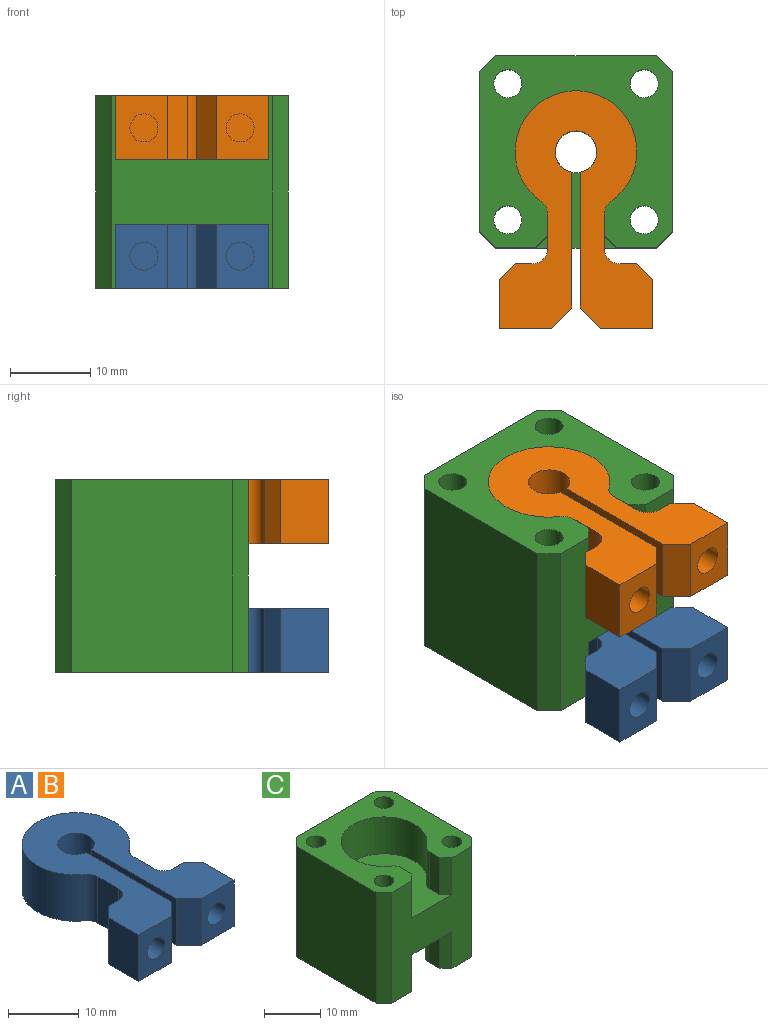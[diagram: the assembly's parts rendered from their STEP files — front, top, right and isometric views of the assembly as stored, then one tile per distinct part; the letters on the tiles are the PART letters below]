
ASSEMBLY  parts=3 mates=3
PART A: 26 faces, bbox 19x29.6x8 mm
  f0: cylinder r=7.6mm len=15.2mm, axis (0,0,1), area 307.8mm2, adj f1,f3,f24,f25
  f1: plane 29.6x19mm, normal (0,0,-1), area 331.4mm2, adj f0,f2,f4,f5,f6,f7,f8,f9
  f2: cylinder r=2.6mm len=8mm, axis (0,0,1), area 122.6mm2, adj f1,f3,f5,f7
  f3: plane 29.6x19mm, normal (0,0,1), area 331.4mm2, adj f0,f2,f4,f5,f6,f7,f8,f9
  f4: plane 8x6.5mm, normal (0,-1,0), area 42.4mm2, adj f1,f3,f11,f20,f23
  f5: plane 16.95x8mm, normal (1,0,0), area 135.6mm2, adj f1,f2,f3,f23
  f6: plane 8x4.13mm, normal (-1,0,0), area 33.1mm2, adj f1,f3,f15,f25
  f7: plane 16.95x8mm, normal (-1,0,0), area 135.6mm2, adj f1,f2,f3,f22
  f8: plane 8x6.5mm, normal (0,-1,0), area 42.4mm2, adj f1,f3,f12,f18,f22
  f9: plane 8x4.13mm, normal (1,0,0), area 33.1mm2, adj f1,f3,f14,f24
  f10: plane 8x2mm, normal (0,1,0), area 16mm2, adj f1,f3,f15,f17
  f11: plane 8x6mm, normal (-1,0,0), area 48mm2, adj f1,f3,f4,f17
  f12: plane 8x6mm, normal (1,0,0), area 48mm2, adj f1,f3,f8,f16
  f13: plane 8x2mm, normal (0,1,0), area 16mm2, adj f1,f3,f14,f16
  f14: cylinder r=2mm len=8mm, axis (0,0,-1), area 25.1mm2, adj f1,f3,f9,f13
  f15: cylinder r=2mm len=8mm, axis (0,0,-1), area 25.1mm2, adj f1,f3,f6,f10
  f16: plane 8x2mm, normal (0.71,0.71,0), area 22.6mm2, adj f1,f3,f12,f13
  f17: plane 8x2mm, normal (-0.71,0.71,0), area 22.6mm2, adj f1,f3,f10,f11
  f18: cylinder r=1.75mm len=5mm, axis (0,-1,0), area 55mm2, adj f8,f19
  f19: plane 3.5x3.5mm, normal (0,-1,0), area 9.6mm2, adj f18
  f20: cylinder r=1.75mm len=5mm, axis (0,-1,0), area 55mm2, adj f4,f21
  f21: plane 3.5x3.5mm, normal (0,-1,0), area 9.6mm2, adj f20
  f22: plane 8x2.5mm, normal (-0.71,-0.71,0), area 28.3mm2, adj f1,f3,f7,f8
  f23: plane 8x2.5mm, normal (0.71,-0.71,0), area 28.3mm2, adj f1,f3,f4,f5
  f24: cylinder r=2mm len=8mm, axis (0,0,1), area 15.4mm2, adj f0,f1,f3,f9
  f25: cylinder r=2mm len=8mm, axis (0,0,1), area 15.4mm2, adj f0,f1,f3,f6
PART B: same geometry as A
PART C: 31 faces, bbox 24x24x24 mm
  f0: cylinder r=2.6mm len=8mm, axis (0,0,-1), area 130.7mm2, adj f13,f20
  f1: plane 24x20mm, normal (0,-1,0), area 320mm2, adj f2,f6,f9,f10,f13,f20,f23,f24
  f2: plane 24x24mm, normal (0,0,-1), area 319.2mm2, adj f1,f3,f4,f5,f7,f8,f9,f10
  f3: plane 24x20mm, normal (-1,0,0), area 480mm2, adj f2,f6,f8,f10
  f4: plane 24x20mm, normal (1,0,0), area 480mm2, adj f2,f6,f7,f9
  f5: plane 24x20mm, normal (0,1,0), area 480mm2, adj f2,f6,f7,f8
  f6: plane 24x24mm, normal (0,0,1), area 312.7mm2, adj f1,f3,f4,f5,f7,f8,f9,f10
  f7: plane 24x2mm, normal (0.71,0.71,0), area 67.9mm2, adj f2,f4,f5,f6
  f8: plane 24x2mm, normal (-0.71,0.71,0), area 67.9mm2, adj f2,f3,f5,f6
  f9: plane 24x2mm, normal (0.71,-0.71,0), area 67.9mm2, adj f1,f2,f4,f6
  f10: plane 24x2mm, normal (-0.71,-0.71,0), area 67.9mm2, adj f1,f2,f3,f6
  f11: plane 8x2.83mm, normal (1,0,0), area 22.7mm2, adj f2,f13,f16,f23
  f12: plane 8x2.83mm, normal (-1,0,0), area 22.7mm2, adj f2,f13,f15,f24
  f13: plane 19.44x14.87mm, normal (0,0,-1), area 189mm2, adj f0,f1,f11,f12,f14,f15,f16,f23
  f14: cylinder r=7.44mm len=14.87mm, axis (0,0,-1), area 299.8mm2, adj f2,f13,f15,f16
  f15: cylinder r=2mm len=8mm, axis (0,0,-1), area 15.2mm2, adj f2,f12,f13,f14
  f16: cylinder r=2mm len=8mm, axis (0,0,-1), area 15.2mm2, adj f2,f11,f13,f14
  f17: cylinder r=7.6mm len=15.2mm, axis (0,0,1), area 307.8mm2, adj f6,f20,f21,f22
  f18: plane 8x2.63mm, normal (1,0,0), area 21.1mm2, adj f6,f20,f21,f25
  f19: plane 8x2.63mm, normal (-1,0,0), area 21.1mm2, adj f6,f20,f22,f26
  f20: plane 19.6x15.2mm, normal (0,0,1), area 195.6mm2, adj f0,f1,f17,f18,f19,f21,f22,f25
  f21: cylinder r=2mm len=8mm, axis (0,0,1), area 15.4mm2, adj f6,f17,f18,f20
  f22: cylinder r=2mm len=8mm, axis (0,0,1), area 15.4mm2, adj f6,f17,f19,f20
  f23: plane 8x1.5mm, normal (0.71,-0.71,0), area 17mm2, adj f1,f2,f11,f13
  f24: plane 8x1.5mm, normal (-0.71,-0.71,0), area 17mm2, adj f1,f2,f12,f13
  f25: plane 8x1.5mm, normal (0.71,-0.71,0), area 17mm2, adj f1,f6,f18,f20
  f26: plane 8x1.5mm, normal (-0.71,-0.71,0), area 17mm2, adj f1,f6,f19,f20
  f27: cylinder r=1.75mm len=24mm, axis (0,0,-1), area 263.9mm2, adj f2,f6
  f28: cylinder r=1.75mm len=24mm, axis (0,0,-1), area 263.9mm2, adj f2,f6
  f29: cylinder r=1.75mm len=24mm, axis (0,0,-1), area 263.9mm2, adj f2,f6
  f30: cylinder r=1.75mm len=24mm, axis (0,0,-1), area 263.9mm2, adj f2,f6
PLACE A t=(-9.8,-0.26,-2.7)mm
PLACE B t=(-9.8,-0.26,13.3)mm
PLACE C t=(-9.8,-0.26,-6.7)mm
MATE cylindrical B.f0 <-> C.f6  axis (0,0,-1) through (-9.8,-0.26,9.3)mm
MATE cylindrical B.f0 <-> C.f0  axis (0,0,1) through (-9.8,-0.26,9.3)mm
MATE cylindrical C.f0 <-> A.f0  axis (0,0,-1) through (-9.8,-0.26,-6.7)mm
